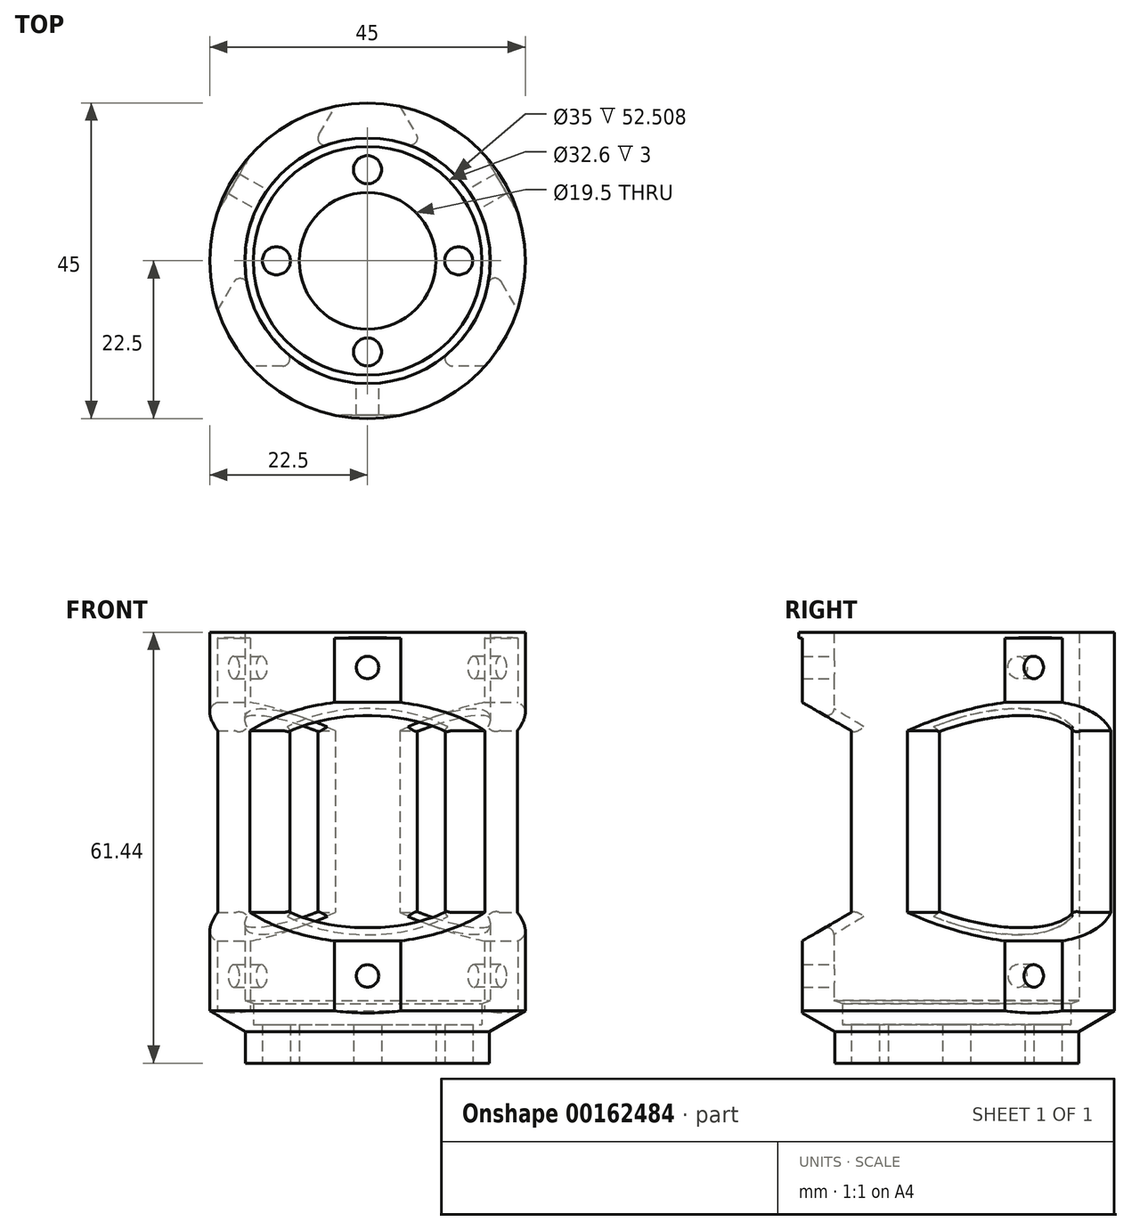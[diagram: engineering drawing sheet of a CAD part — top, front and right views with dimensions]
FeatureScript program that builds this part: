
annotation { "Feature Type Name" : "Feature", "Feature Type Description" : "" }
export const myFeature = defineFeature(function(context is Context, id is Id, definition is map)
    precondition{}
    {
        {
            var Q0;
            Q0=qCreatedBy(makeId("Right.planeOp"),FACE);
            var sketch = newSketch(context, id + "F0", { "sketchPlane" : qUnion([Q0])});
            skLineSegment(sketch, "E0", {"start": v(0, 0) * mm, "end": v(-16.3, 0) * mm});
            skLineSegment(sketch, "E1", {"start": v(-16.3, 0) * mm, "end": v(-16.3, 3) * mm});
            skLineSegment(sketch, "E2", {"start": v(-16.3, 3) * mm, "end": v(-17.5, 3.44) * mm});
            skLineSegment(sketch, "E3", {"start": v(-17.5, 3.44) * mm, "end": v(-17.5, 55.94) * mm});
            skLineSegment(sketch, "E4", {"start": v(0, 0) * mm, "end": v(0, -5.5) * mm});
            skLineSegment(sketch, "E5", {"start": v(0, -5.5) * mm, "end": v(-17.4, -5.5) * mm});
            skLineSegment(sketch, "E6", {"start": v(-17.4, -5.5) * mm, "end": v(-17.4, -1) * mm});
            skLineSegment(sketch, "E7", {"start": v(-17.4, -1) * mm, "end": v(-22.5, 1.94) * mm});
            skLineSegment(sketch, "E8", {"start": v(-17.5, 55.94) * mm, "end": v(-22.5, 55.94) * mm});
            skLineSegment(sketch, "E9", {"start": v(-22.5, 55.94) * mm, "end": v(-22.5, 1.94) * mm});
            skLineSegment(sketch, "E10", {"start": v(0, 0) * mm, "end": v(0, 46.6) * mm, "construction": true});
            skSolve(sketch);
        }
        {
            var Q0;
            Q0 = qSketchRegion(id + "F0", true);
            var Q1;
            Q1=sQuery(id+"F0.wireOp",EDGE,"E10");
            revolve(context, id + "F1", {"entities" : qUnion([Q0]), "axis" : qUnion([Q1]), "revolveType" : RevolveType.FULL});
        }
        {
            var Q0;
            Q0=makeQuery(id+"F1.opRevolve","SWEPT_FACE",FACE,{"disambiguationData":[OSD([sQuery(id+"F0.wireOp",EDGE,"E5")])]});
            var sketch = newSketch(context, id + "F2", { "sketchPlane" : qUnion([Q0])});
            skCircle(sketch, "E11", {"center": v(0, 13) * mm, "radius": 2 * mm});
            skCircle(sketch, "E12", {"center": v(13, 0) * mm, "radius": 2 * mm});
            skLineSegment(sketch, "E13", {"start": v(0, 0) * mm, "end": v(40.72, 0) * mm, "construction": true});
            skLineSegment(sketch, "E14", {"start": v(0, 0) * mm, "end": v(0, 46.44) * mm, "construction": true});
            skCircle(sketch, "E15.MirrorC", {"center": v(-13, 0) * mm, "radius": 2 * mm});
            skCircle(sketch, "E16.MirrorC", {"center": v(0, -13) * mm, "radius": 2 * mm});
            skCircle(sketch, "E17", {"center": v(0, 0) * mm, "radius": 9.75 * mm});
            skSolve(sketch);
        }
        {
            var Q0;
            Q0 = qSketchRegion(id + "F2", true);
            extrude(context, id + "F3", {"entities" : qUnion([Q0]), "operationType" : NewBodyOperationType.REMOVE, "endBound" : BoundingType.THROUGH_ALL, "oppositeDirection" : true, "depth" : 25 * mm});
        }
        {
            var Q0;
            Q0=qCreatedBy(makeId("Right.planeOp"),FACE);
            var sketch = newSketch(context, id + "F4", { "sketchPlane" : qUnion([Q0])});
            skLineSegment(sketch, "E18", {"start": v(-22, 55.1) * mm, "end": v(-22, 45.94) * mm});
            skLineSegment(sketch, "E19", {"start": v(-22, 45.94) * mm, "end": v(-15, 41.9) * mm});
            skLineSegment(sketch, "E20", {"start": v(-15, 41.9) * mm, "end": v(-15, 15.99) * mm});
            skLineSegment(sketch, "E21", {"start": v(-15, 15.99) * mm, "end": v(-22, 11.94) * mm});
            skLineSegment(sketch, "E22", {"start": v(-22, 11.94) * mm, "end": v(-22, -3.06) * mm});
            skLineSegment(sketch, "E23", {"start": v(-22, -3.06) * mm, "end": v(-41.5, -1.06) * mm});
            skLineSegment(sketch, "E24", {"start": v(-41.5, -1.06) * mm, "end": v(-41.5, 57.6) * mm});
            skLineSegment(sketch, "E25", {"start": v(-41.5, 57.6) * mm, "end": v(-22, 55.1) * mm});
            skSolve(sketch);
        }
        {
            var Q0;
            Q0 = qSketchRegion(id + "F4", true);
            extrude(context, id + "F5", {"entities" : qUnion([Q0]), "endBound" : BoundingType.SYMMETRIC, "depth" : 60 * mm});
        }
        {
            var Q0;
            Q0=makeQuery(id+"F5.opExtrude","SWEPT_BODY",BODY,{"disambiguationData":[OSD([sQuery(id+"F4.wireOp",EDGE,"E18"),sQuery(id+"F4.wireOp",EDGE,"E19"),sQuery(id+"F4.wireOp",EDGE,"E20"),sQuery(id+"F4.wireOp",EDGE,"E21"),sQuery(id+"F4.wireOp",EDGE,"E22"),sQuery(id+"F4.wireOp",EDGE,"E23"),sQuery(id+"F4.wireOp",EDGE,"E24"),sQuery(id+"F4.wireOp",EDGE,"E25")])]});
            var Q1;
            Q1=makeQuery(id+"F1.opRevolve","SWEPT_FACE",FACE,{"disambiguationData":[OSD([sQuery(id+"F0.wireOp",EDGE,"E3")])]});
            circularPattern(context, id + "F6", {"entities" : qUnion([Q0]), "axis" : qUnion([Q1]), "angle" : 120 * degree, "instanceCount" : 3});
        }
        {
            var Q0;
            Q0=makeQuery(id+"F6.opPattern","COPY",BODY,{"derivedFrom":makeQuery(id+"F5.opExtrude","SWEPT_BODY",BODY,{"disambiguationData":[OSD([sQuery(id+"F4.wireOp",EDGE,"E18"),sQuery(id+"F4.wireOp",EDGE,"E19"),sQuery(id+"F4.wireOp",EDGE,"E20"),sQuery(id+"F4.wireOp",EDGE,"E21"),sQuery(id+"F4.wireOp",EDGE,"E22"),sQuery(id+"F4.wireOp",EDGE,"E23"),sQuery(id+"F4.wireOp",EDGE,"E24"),sQuery(id+"F4.wireOp",EDGE,"E25")])]}),"instanceName":"1"});
            var Q1;
            Q1=makeQuery(id+"F5.opExtrude","SWEPT_BODY",BODY,{"disambiguationData":[OSD([sQuery(id+"F4.wireOp",EDGE,"E18"),sQuery(id+"F4.wireOp",EDGE,"E19"),sQuery(id+"F4.wireOp",EDGE,"E20"),sQuery(id+"F4.wireOp",EDGE,"E21"),sQuery(id+"F4.wireOp",EDGE,"E22"),sQuery(id+"F4.wireOp",EDGE,"E23"),sQuery(id+"F4.wireOp",EDGE,"E24"),sQuery(id+"F4.wireOp",EDGE,"E25")])]});
            var Q2;
            Q2=makeQuery(id+"F6.opPattern","COPY",BODY,{"derivedFrom":makeQuery(id+"F5.opExtrude","SWEPT_BODY",BODY,{"disambiguationData":[OSD([sQuery(id+"F4.wireOp",EDGE,"E18"),sQuery(id+"F4.wireOp",EDGE,"E19"),sQuery(id+"F4.wireOp",EDGE,"E20"),sQuery(id+"F4.wireOp",EDGE,"E21"),sQuery(id+"F4.wireOp",EDGE,"E22"),sQuery(id+"F4.wireOp",EDGE,"E23"),sQuery(id+"F4.wireOp",EDGE,"E24"),sQuery(id+"F4.wireOp",EDGE,"E25")])]}),"instanceName":"2"});
            var Q3;
            Q3=makeQuery(id+"F1.opRevolve","SWEPT_BODY",BODY,{"disambiguationData":[OSD([sQuery(id+"F0.wireOp",EDGE,"E0"),sQuery(id+"F0.wireOp",EDGE,"E1"),sQuery(id+"F0.wireOp",EDGE,"E2"),sQuery(id+"F0.wireOp",EDGE,"E3"),sQuery(id+"F0.wireOp",EDGE,"E4"),sQuery(id+"F0.wireOp",EDGE,"E5"),sQuery(id+"F0.wireOp",EDGE,"E6"),sQuery(id+"F0.wireOp",EDGE,"E7"),sQuery(id+"F0.wireOp",EDGE,"E8"),sQuery(id+"F0.wireOp",EDGE,"E9")])]});
            booleanBodies(context, id + "F7", {"operationType" : BooleanOperationType.SUBTRACTION, "tools" : qUnion([Q0, Q1, Q2]), "targets" : qUnion([Q3])});
        }
        {
            var Q0;
            Q0=makeQuery(id+"F7.opBoolean","COPY",FACE,{"derivedFrom":makeQuery(id+"F5.opExtrude","SWEPT_FACE",FACE,{"disambiguationData":[OSD([sQuery(id+"F4.wireOp",EDGE,"E18")])]})});
            var sketch = newSketch(context, id + "F8", { "sketchPlane" : qUnion([Q0])});
            skCircle(sketch, "E26", {"center": v(0, 50.94) * mm, "radius": 1.6 * mm});
            skCircle(sketch, "E27", {"center": v(0, 6.94) * mm, "radius": 1.6 * mm});
            skSolve(sketch);
        }
        {
            var Q0;
            Q0 = qSketchRegion(id + "F8", true);
            extrude(context, id + "F9", {"entities" : qUnion([Q0]), "endBound" : BoundingType.SYMMETRIC, "depth" : 10 * mm});
        }
        {
            var Q0;
            Q0=makeQuery(id+"F9.opExtrude","SWEPT_BODY",BODY,{"disambiguationData":[OSD([sQuery(id+"F8.wireOp",EDGE,"E26")])]});
            var Q1;
            Q1=makeQuery(id+"F9.opExtrude","SWEPT_BODY",BODY,{"disambiguationData":[OSD([sQuery(id+"F8.wireOp",EDGE,"E27")])]});
            var Q2;
            Q2=makeQuery(id+"F1.opRevolve","SWEPT_FACE",FACE,{"disambiguationData":[OSD([sQuery(id+"F0.wireOp",EDGE,"E3")])]});
            circularPattern(context, id + "F10", {"entities" : qUnion([Q0, Q1]), "axis" : qUnion([Q2]), "angle" : 120 * degree, "instanceCount" : 3});
        }
        {
            var Q0;
            Q0=makeQuery(id+"F9.opExtrude","SWEPT_BODY",BODY,{"disambiguationData":[OSD([sQuery(id+"F8.wireOp",EDGE,"E26")])]});
            var Q1;
            Q1=makeQuery(id+"F9.opExtrude","SWEPT_BODY",BODY,{"disambiguationData":[OSD([sQuery(id+"F8.wireOp",EDGE,"E27")])]});
            var Q2;
            Q2=makeQuery(id+"F10.opPattern","COPY",BODY,{"derivedFrom":makeQuery(id+"F9.opExtrude","SWEPT_BODY",BODY,{"disambiguationData":[OSD([sQuery(id+"F8.wireOp",EDGE,"E26")])]}),"instanceName":"1"});
            var Q3;
            Q3=makeQuery(id+"F10.opPattern","COPY",BODY,{"derivedFrom":makeQuery(id+"F9.opExtrude","SWEPT_BODY",BODY,{"disambiguationData":[OSD([sQuery(id+"F8.wireOp",EDGE,"E27")])]}),"instanceName":"1"});
            var Q4;
            Q4=makeQuery(id+"F10.opPattern","COPY",BODY,{"derivedFrom":makeQuery(id+"F9.opExtrude","SWEPT_BODY",BODY,{"disambiguationData":[OSD([sQuery(id+"F8.wireOp",EDGE,"E26")])]}),"instanceName":"2"});
            var Q5;
            Q5=makeQuery(id+"F10.opPattern","COPY",BODY,{"derivedFrom":makeQuery(id+"F9.opExtrude","SWEPT_BODY",BODY,{"disambiguationData":[OSD([sQuery(id+"F8.wireOp",EDGE,"E27")])]}),"instanceName":"2"});
            var Q6;
            Q6=makeQuery(id+"F1.opRevolve","SWEPT_BODY",BODY,{"disambiguationData":[OSD([sQuery(id+"F0.wireOp",EDGE,"E0"),sQuery(id+"F0.wireOp",EDGE,"E1"),sQuery(id+"F0.wireOp",EDGE,"E2"),sQuery(id+"F0.wireOp",EDGE,"E3"),sQuery(id+"F0.wireOp",EDGE,"E4"),sQuery(id+"F0.wireOp",EDGE,"E5"),sQuery(id+"F0.wireOp",EDGE,"E6"),sQuery(id+"F0.wireOp",EDGE,"E7"),sQuery(id+"F0.wireOp",EDGE,"E8"),sQuery(id+"F0.wireOp",EDGE,"E9")])]});
            booleanBodies(context, id + "F11", {"operationType" : BooleanOperationType.SUBTRACTION, "tools" : qUnion([Q0, Q1, Q2, Q3, Q4, Q5]), "targets" : qUnion([Q6])});
        }
        {
            var Q0;
            Q0=makeQuery(id+"F7.opBoolean","INTERSECT",EDGE,{"disambiguationData":[OD(1.0)],"derivedFrom":[makeQuery(id+"F1.opRevolve","SWEPT_FACE",FACE,{"disambiguationData":[OSD([sQuery(id+"F0.wireOp",EDGE,"E3")])]}),makeQuery(id+"F6.opPattern","COPY",FACE,{"derivedFrom":makeQuery(id+"F5.opExtrude","SWEPT_FACE",FACE,{"disambiguationData":[OSD([sQuery(id+"F4.wireOp",EDGE,"E20")])]}),"instanceName":"2"})]});
            var Q1;
            Q1=makeQuery(id+"F7.opBoolean","INTERSECT",EDGE,{"derivedFrom":[makeQuery(id+"F1.opRevolve","SWEPT_FACE",FACE,{"disambiguationData":[OSD([sQuery(id+"F0.wireOp",EDGE,"E3")])]}),makeQuery(id+"F6.opPattern","COPY",FACE,{"derivedFrom":makeQuery(id+"F5.opExtrude","SWEPT_FACE",FACE,{"disambiguationData":[OSD([sQuery(id+"F4.wireOp",EDGE,"E19")])]}),"instanceName":"2"})]});
            var Q2;
            Q2=makeQuery(id+"F7.opBoolean","INTERSECT",EDGE,{"disambiguationData":[OD(0.0)],"derivedFrom":[makeQuery(id+"F1.opRevolve","SWEPT_FACE",FACE,{"disambiguationData":[OSD([sQuery(id+"F0.wireOp",EDGE,"E3")])]}),makeQuery(id+"F6.opPattern","COPY",FACE,{"derivedFrom":makeQuery(id+"F5.opExtrude","SWEPT_FACE",FACE,{"disambiguationData":[OSD([sQuery(id+"F4.wireOp",EDGE,"E20")])]}),"instanceName":"2"})]});
            var Q3;
            Q3=makeQuery(id+"F7.opBoolean","INTERSECT",EDGE,{"derivedFrom":[makeQuery(id+"F1.opRevolve","SWEPT_FACE",FACE,{"disambiguationData":[OSD([sQuery(id+"F0.wireOp",EDGE,"E3")])]}),makeQuery(id+"F6.opPattern","COPY",FACE,{"derivedFrom":makeQuery(id+"F5.opExtrude","SWEPT_FACE",FACE,{"disambiguationData":[OSD([sQuery(id+"F4.wireOp",EDGE,"E21")])]}),"instanceName":"2"})]});
            var Q4;
            Q4=makeQuery(id+"F7.opBoolean","INTERSECT",EDGE,{"derivedFrom":[makeQuery(id+"F1.opRevolve","SWEPT_FACE",FACE,{"disambiguationData":[OSD([sQuery(id+"F0.wireOp",EDGE,"E3")])]}),makeQuery(id+"F5.opExtrude","SWEPT_FACE",FACE,{"disambiguationData":[OSD([sQuery(id+"F4.wireOp",EDGE,"E21")])]})]});
            var Q5;
            Q5=makeQuery(id+"F7.opBoolean","INTERSECT",EDGE,{"disambiguationData":[OD(0.0)],"derivedFrom":[makeQuery(id+"F1.opRevolve","SWEPT_FACE",FACE,{"disambiguationData":[OSD([sQuery(id+"F0.wireOp",EDGE,"E3")])]}),makeQuery(id+"F5.opExtrude","SWEPT_FACE",FACE,{"disambiguationData":[OSD([sQuery(id+"F4.wireOp",EDGE,"E20")])]})]});
            var Q6;
            Q6=makeQuery(id+"F7.opBoolean","INTERSECT",EDGE,{"disambiguationData":[OD(1.0)],"derivedFrom":[makeQuery(id+"F1.opRevolve","SWEPT_FACE",FACE,{"disambiguationData":[OSD([sQuery(id+"F0.wireOp",EDGE,"E3")])]}),makeQuery(id+"F5.opExtrude","SWEPT_FACE",FACE,{"disambiguationData":[OSD([sQuery(id+"F4.wireOp",EDGE,"E20")])]})]});
            var Q7;
            Q7=makeQuery(id+"F7.opBoolean","INTERSECT",EDGE,{"derivedFrom":[makeQuery(id+"F1.opRevolve","SWEPT_FACE",FACE,{"disambiguationData":[OSD([sQuery(id+"F0.wireOp",EDGE,"E3")])]}),makeQuery(id+"F5.opExtrude","SWEPT_FACE",FACE,{"disambiguationData":[OSD([sQuery(id+"F4.wireOp",EDGE,"E19")])]})]});
            var Q8;
            Q8=makeQuery(id+"F7.opBoolean","INTERSECT",EDGE,{"disambiguationData":[OD(0.0)],"derivedFrom":[makeQuery(id+"F1.opRevolve","SWEPT_FACE",FACE,{"disambiguationData":[OSD([sQuery(id+"F0.wireOp",EDGE,"E3")])]}),makeQuery(id+"F6.opPattern","COPY",FACE,{"derivedFrom":makeQuery(id+"F5.opExtrude","SWEPT_FACE",FACE,{"disambiguationData":[OSD([sQuery(id+"F4.wireOp",EDGE,"E20")])]}),"instanceName":"1"})]});
            var Q9;
            Q9=makeQuery(id+"F7.opBoolean","INTERSECT",EDGE,{"derivedFrom":[makeQuery(id+"F1.opRevolve","SWEPT_FACE",FACE,{"disambiguationData":[OSD([sQuery(id+"F0.wireOp",EDGE,"E3")])]}),makeQuery(id+"F6.opPattern","COPY",FACE,{"derivedFrom":makeQuery(id+"F5.opExtrude","SWEPT_FACE",FACE,{"disambiguationData":[OSD([sQuery(id+"F4.wireOp",EDGE,"E19")])]}),"instanceName":"1"})]});
            var Q10;
            Q10=makeQuery(id+"F7.opBoolean","INTERSECT",EDGE,{"disambiguationData":[OD(1.0)],"derivedFrom":[makeQuery(id+"F1.opRevolve","SWEPT_FACE",FACE,{"disambiguationData":[OSD([sQuery(id+"F0.wireOp",EDGE,"E3")])]}),makeQuery(id+"F6.opPattern","COPY",FACE,{"derivedFrom":makeQuery(id+"F5.opExtrude","SWEPT_FACE",FACE,{"disambiguationData":[OSD([sQuery(id+"F4.wireOp",EDGE,"E20")])]}),"instanceName":"1"})]});
            var Q11;
            Q11=makeQuery(id+"F7.opBoolean","INTERSECT",EDGE,{"derivedFrom":[makeQuery(id+"F1.opRevolve","SWEPT_FACE",FACE,{"disambiguationData":[OSD([sQuery(id+"F0.wireOp",EDGE,"E3")])]}),makeQuery(id+"F6.opPattern","COPY",FACE,{"derivedFrom":makeQuery(id+"F5.opExtrude","SWEPT_FACE",FACE,{"disambiguationData":[OSD([sQuery(id+"F4.wireOp",EDGE,"E21")])]}),"instanceName":"1"})]});
            fillet(context, id + "F12", {"entities" : qUnion([Q0, Q1, Q2, Q3, Q4, Q5, Q6, Q7, Q8, Q9, Q10, Q11]), "radius" : 1 * mm, "tangentPropagation" : true, "allowEdgeOverflow" : false});
        }
    });
